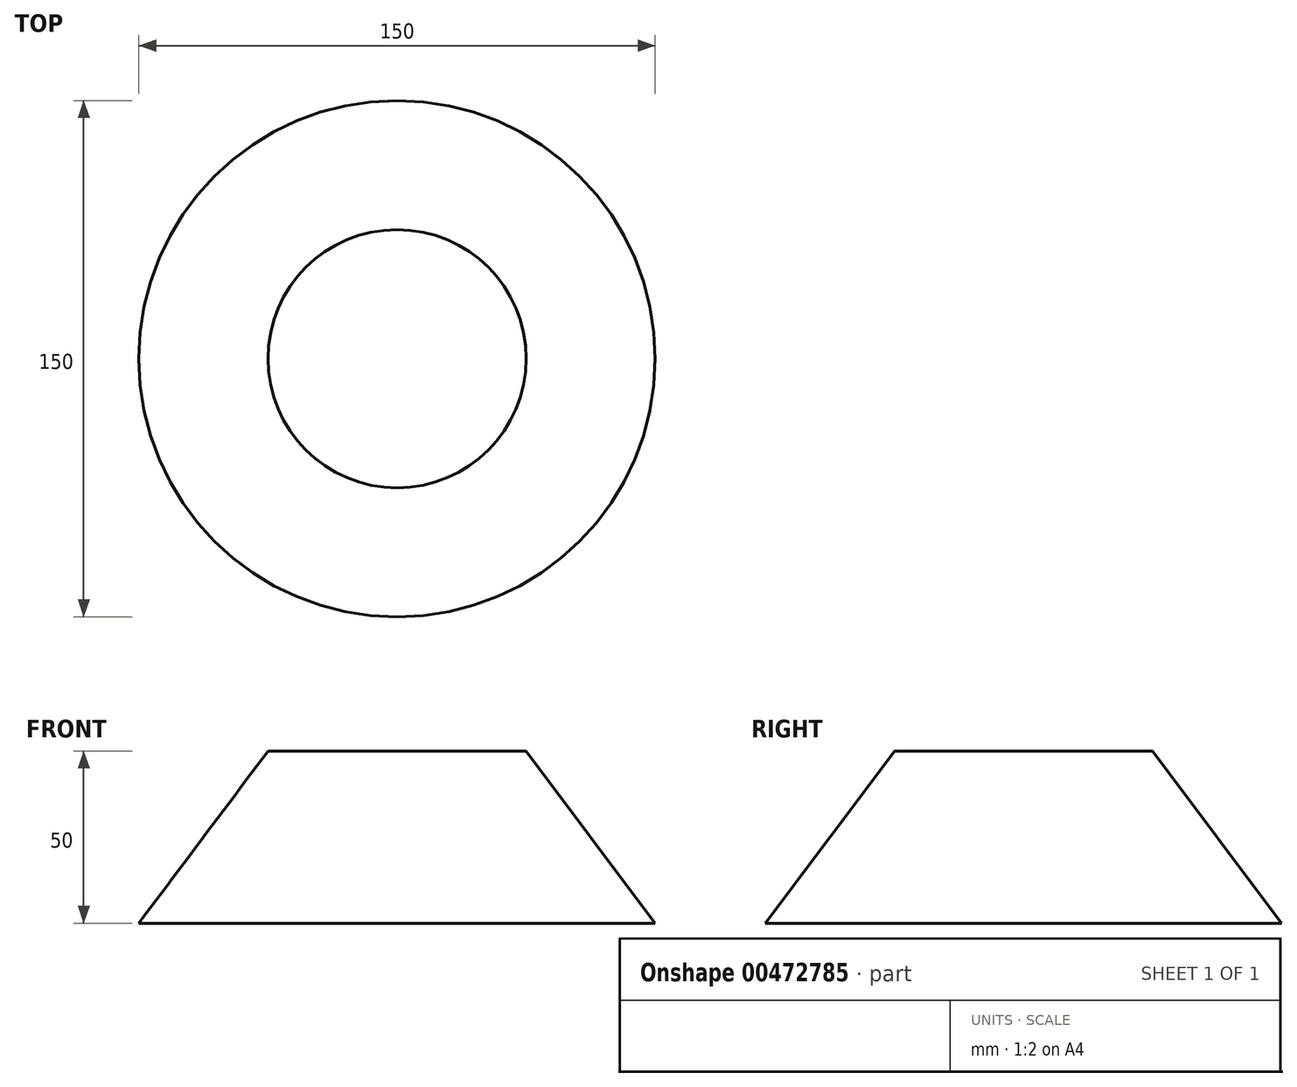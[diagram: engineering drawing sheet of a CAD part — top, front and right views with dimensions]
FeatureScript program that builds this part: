
annotation { "Feature Type Name" : "Feature", "Feature Type Description" : "" }
export const myFeature = defineFeature(function(context is Context, id is Id, definition is map)
    precondition{}
    {
        {
            var Q0;
            Q0=qCreatedBy(makeId("Front.planeOp"),FACE);
            var sketch = newSketch(context, id + "F0", { "sketchPlane" : qUnion([Q0])});
            skLineSegment(sketch, "E0", {"start": v(0, 0) * mm, "end": v(0, 50) * mm});
            skLineSegment(sketch, "E1", {"start": v(0, 50) * mm, "end": v(-37.5, 50) * mm});
            skLineSegment(sketch, "E2", {"start": v(0, 0) * mm, "end": v(-75, 0) * mm});
            skLineSegment(sketch, "E3", {"start": v(-75, 0) * mm, "end": v(-37.5, 50) * mm});
            skSolve(sketch);
        }
        {
            var Q0;
            Q0=makeQuery(id+"F0.imprint","IMPRINT",FACE,{"disambiguationData":[TD([[makeQuery(id+"F0.imprint","IMPRINT",EDGE,{"derivedFrom":sQuery(id+"F0.wireOp",EDGE,"E0")}),1.0]])]});
            var Q1;
            Q1=sQuery(id+"F0.wireOp",EDGE,"E0");
            revolve(context, id + "F1", {"entities" : qUnion([Q0]), "axis" : qUnion([Q1]), "revolveType" : RevolveType.FULL});
        }
    });
